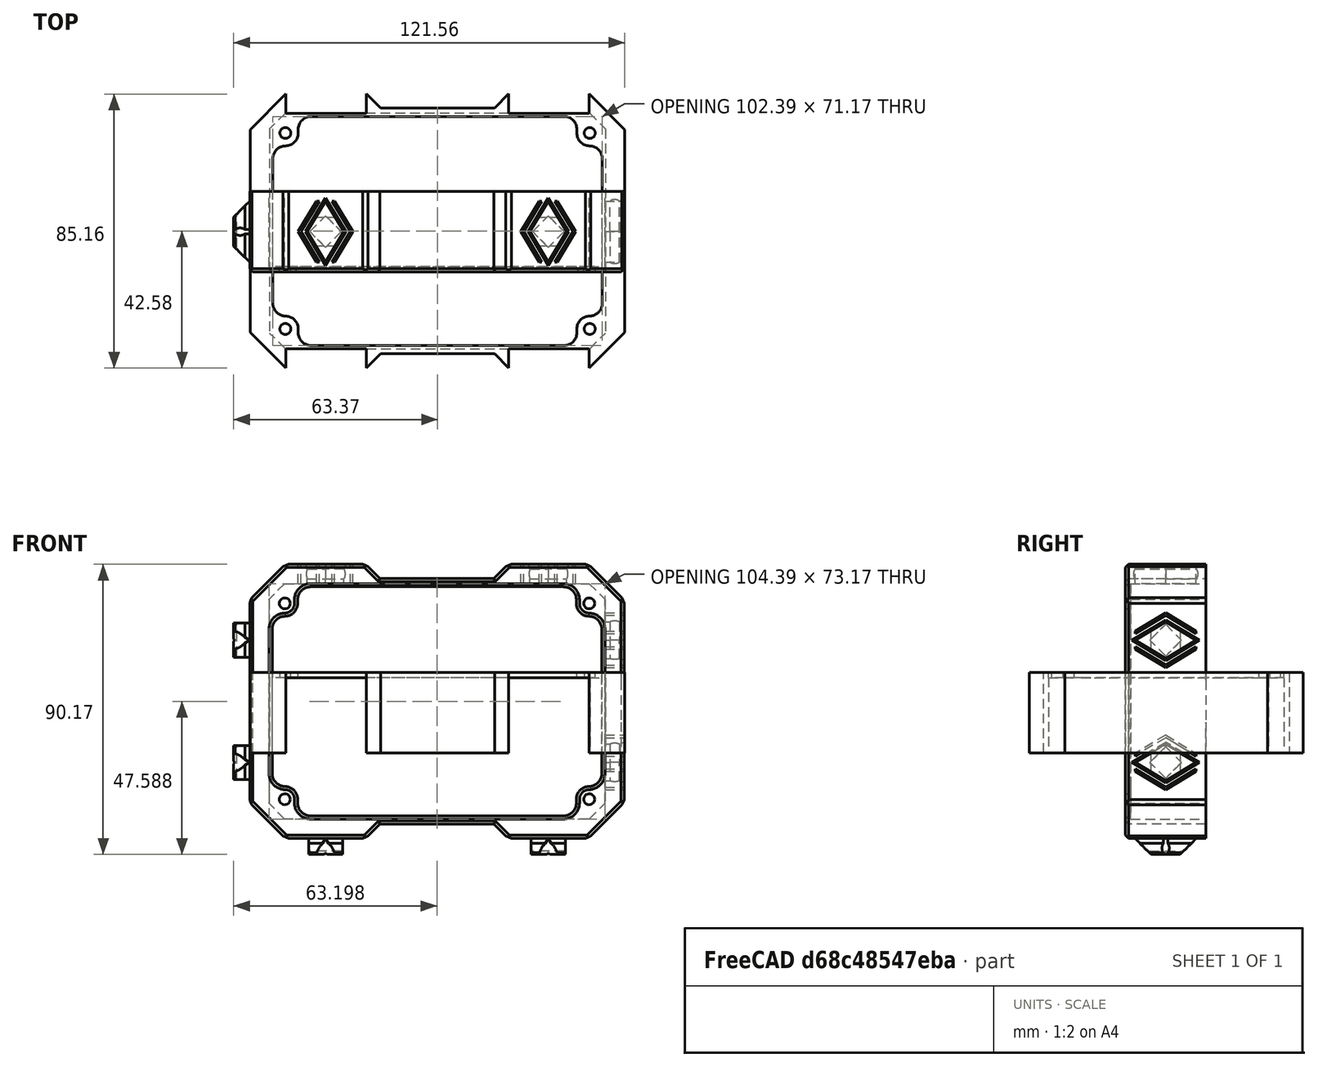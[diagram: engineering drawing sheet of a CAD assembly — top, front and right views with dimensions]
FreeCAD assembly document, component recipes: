
FREECAD ASSEMBLY — COMPONENT RECIPES ("K97-120_DockLink-Frame_front")

This assembly document has 3 components, labeled P0..P2 below (a component is one placed body or linked part). 3 of them carry a construction recipe — the FreeCAD feature program that regenerates the part from scratch, quoted from this document or its linked companion documents; the rest are supplied as boundary geometry only. No exploded tour is included for this assembly.
COMPONENT P0 — recipe-attached ("Body001", modeled in this document).
Construction recipe (the document's own serialized feature program — sketch geometry with constraints, then the solid features built on it; lengths are millimeters unless a unit is written):

FEATURE [Sketcher::SketchObject] Sketch
  ArcFitTolerance = 1e-06
  ExternalTypes = [0]
  FullyConstrained = true
  MakeInternals = false
  Placement = pos=(0,0,0.75) rot=(0,0,1;0rad)
  sketch-geometry (16):
    g0: ArcOfCircle [constr] CenterX=49.99 CenterY=30.66 CenterZ=0 NormalX=0 NormalY=0 NormalZ=1 AngleXU=0 Radius=2.00394 StartAngle=0.00171116 EndAngle=0.785083
    g1: LineSegment [constr] StartX=51.4075 StartY=32.0766 StartZ=0 EndX=47.58 EndY=35.9 EndZ=0
    g2: ArcOfCircle [constr] CenterX=46.17 CenterY=34.49 CenterZ=0 NormalX=0 NormalY=0 NormalZ=1 AngleXU=0 Radius=1.99404 StartAngle=0.785398 EndAngle=1.57287
    g3: LineSegment [constr] StartX=46.1659 StartY=36.484 StartZ=0 EndX=0 EndY=36.484 EndZ=0
    g4: LineSegment [constr] StartX=51.9939 StartY=30.6634 StartZ=0 EndX=51.9939 EndY=0 EndZ=0
    g5: Circle [constr] CenterX=47.29 CenterY=30.44 CenterZ=0 NormalX=0 NormalY=0 NormalZ=1 AngleXU=0 Radius=1.7
    g6: LineSegment StartX=0 StartY=38.184 StartZ=0 EndX=17.7 EndY=38.184 EndZ=0
    g7: LineSegment StartX=17.7 StartY=38.184 StartZ=0 EndX=22.1 EndY=42.584 EndZ=0
    g8: LineSegment StartX=22.1 StartY=42.584 StartZ=0 EndX=47.1 EndY=42.584 EndZ=0
    g9: LineSegment StartX=0 StartY=38.184 StartZ=0 EndX=0 EndY=36.584 EndZ=0
    g10: LineSegment StartX=0 StartY=36.584 StartZ=0 EndX=47.3197 EndY=36.584 EndZ=0
    g11: LineSegment StartX=47.3197 StartY=36.584 StartZ=0 EndX=52.1939 EndY=31.7149 EndZ=0
    g12: LineSegment StartX=52.1939 StartY=31.7149 StartZ=0 EndX=52.1939 EndY=0 EndZ=0
    g13: LineSegment StartX=47.1 StartY=42.584 StartZ=0 EndX=58.1939 EndY=31.5017 EndZ=0
    g14: LineSegment StartX=58.1939 StartY=31.5017 StartZ=0 EndX=58.1939 EndY=0 EndZ=0
    g15: LineSegment StartX=52.1939 StartY=0 StartZ=0 EndX=58.1939 EndY=0 EndZ=0
  constraints (53):
    c: Coincident(g1,g2)
    c: Coincident(g0,g1)
    c: Coincident(g3,g2)
    c: PointOnObject(g3,g-2)
    c: Horizontal(g3)
    c: Coincident(g4,g0)
    c: PointOnObject(g4,g-1)
    c: Vertical(g4)
    c: Distance(g5,g-1) = 30.44
    c: Distance(g5,g-2) = 47.29
    c: Diameter(g5) = 3.4
    c: Distance(g0,g-1) = 30.66
    c: Distance(g0,g-2) = 49.99
    c: Distance(g2,g-2) = 46.17
    c: Distance(g2,g-1) = 34.49
    c: Distance(g2,g1) = 1.53
    c: Distance(g0,g0) = 1.53
    c: Distance(g1,g1) = 5.41
    c: Angle(g1,g-1) = 0.784875
    c: Distance(g1,g-1) = 35.9
    c: Distance(g1,g-2) = 47.58
    c: PointOnObject(g6,g-2)
    c: Horizontal(g6)
    c: Coincident(g7,g6)
    c: Coincident(g8,g7)
    c: Horizontal(g8)
    c: Coincident(g9,g6)
    c: PointOnObject(g9,g-2)
    c: Coincident(g10,g9)
    c: Horizontal(g10)
    c: Coincident(g11,g10)
    c: Coincident(g12,g11)
    c: PointOnObject(g12,g-1)
    c: Vertical(g12)
    c: Distance(g12,g4) = 0.2
    c: Parallel(g11,g1)
    c: DistanceY(g9,g9) = 1.6
    c: Coincident(g13,g8)
    c: Coincident(g14,g13)
    c: PointOnObject(g14,g-1)
    c: Vertical(g14)
    c: Coincident(g15,g12)
    c: Coincident(g15,g14)
    c: DistanceX(g15,g15) = 6
    c: Parallel(g11,g13)
    c: Angle(g7,g6) = 2.35619
    c: Distance(g10,g8) = 6
    c: DistanceX(g8,g8) = 25
    c: Distance(g3,g10) = 0.1
    c: Distance(g11,g1) = 0.3
    c: DistanceX(g-1,g8) = 47.1
    c: Distance(g5,g-2) = 47.29
    c: Distance(g5,g-1) = 30.44
FEATURE [PartDesign::Pad] Pad
  Direction = (0,0,1)
  Length = 23.4
  Length2 = 10
  Placement = pos=(0,0,0.75) rot=(0,0,1;0rad)
  Profile = -> Sketch
  ReferenceAxis = -> Sketch [N_Axis]
  Refine = true
  Reversed = true
  SideType = 0
  Suppressed = false
  Type = 0
  Type2 = 0
FEATURE [PartDesign::Mirrored] Mirrored
  BaseFeature = -> Pad
  MirrorPlane = -> XZ_Plane
  Placement = pos=(0,0,0.75) rot=(0,0,1;0rad)
  Refine = true
  Suppressed = false
  TransformMode = 1
FEATURE [PartDesign::Mirrored] Mirrored001
  BaseFeature = -> Mirrored
  MirrorPlane = -> YZ_Plane
  Originals = -> [Mirrored]
  Placement = pos=(0,0,0.75) rot=(0,0,1;0rad)
  Refine = true
  Suppressed = false
  TransformMode = 1
FEATURE [Sketcher::SketchObject] Sketch001
  ArcFitTolerance = 1e-06
  AttachmentSupport = -> [Mirrored001]
  ExternalGeometry = -> [Mirrored001]
  ExternalTypes = [0,0,0,0,0,0,0,0,0,0,0,0,0,0,0,0]
  FullyConstrained = true
  MakeInternals = false
  MapMode = 5
  Placement = pos=(0,0,0.75) rot=(0,0,1;0rad)
  sketch-geometry (25):
    g0: LineSegment [constr] StartX=-47.29 StartY=30.44 StartZ=0 EndX=-47.29 EndY=-30.44 EndZ=0
    g1: LineSegment [constr] StartX=-47.29 StartY=-30.44 StartZ=0 EndX=47.29 EndY=-30.44 EndZ=0
    g2: LineSegment [constr] StartX=47.29 StartY=-30.44 StartZ=0 EndX=47.29 EndY=30.44 EndZ=0
    g3: LineSegment [constr] StartX=47.29 StartY=30.44 StartZ=0 EndX=-47.29 EndY=30.44 EndZ=0
    g4: GeomPoint [constr] X=0 Y=0 Z=0
    g5: Circle CenterX=47.29 CenterY=30.44 CenterZ=0 NormalX=0 NormalY=0 NormalZ=1 AngleXU=0 Radius=1.7
    g6: Circle CenterX=47.29 CenterY=-30.44 CenterZ=0 NormalX=0 NormalY=0 NormalZ=1 AngleXU=0 Radius=1.7
    g7: Circle CenterX=-47.29 CenterY=-30.44 CenterZ=0 NormalX=0 NormalY=0 NormalZ=1 AngleXU=0 Radius=1.7
    g8: Circle CenterX=-47.29 CenterY=30.44 CenterZ=0 NormalX=0 NormalY=0 NormalZ=1 AngleXU=0 Radius=1.7
    g9: ArcOfCircle CenterX=-47.29 CenterY=30.44 CenterZ=0 NormalX=0 NormalY=0 NormalZ=1 AngleXU=0 Radius=4 StartAngle=4.71239 EndAngle=6.28319
    g10: ArcOfCircle CenterX=47.29 CenterY=30.44 CenterZ=0 NormalX=0 NormalY=0 NormalZ=1 AngleXU=0 Radius=4 StartAngle=3.14159 EndAngle=4.71239
    g11: ArcOfCircle CenterX=47.29 CenterY=-30.44 CenterZ=0 NormalX=0 NormalY=0 NormalZ=1 AngleXU=0 Radius=4 StartAngle=1.5708 EndAngle=3.14159
    g12: ArcOfCircle CenterX=-47.29 CenterY=-30.44 CenterZ=0 NormalX=0 NormalY=0 NormalZ=1 AngleXU=0 Radius=4 StartAngle=0 EndAngle=1.5708
    g13: LineSegment StartX=-43.29 StartY=30.44 StartZ=0 EndX=-43.29 EndY=35.584 EndZ=0
    g14: LineSegment StartX=-43.29 StartY=35.584 StartZ=0 EndX=43.29 EndY=35.584 EndZ=0
    g15: LineSegment StartX=43.29 StartY=35.584 StartZ=0 EndX=43.29 EndY=30.44 EndZ=0
    g16: LineSegment StartX=47.29 StartY=26.44 StartZ=0 EndX=51.1939 EndY=26.44 EndZ=0
    g17: LineSegment StartX=47.29 StartY=-26.44 StartZ=0 EndX=51.1939 EndY=-26.44 EndZ=0
    g18: LineSegment StartX=51.1939 StartY=-26.44 StartZ=0 EndX=51.1939 EndY=26.44 EndZ=0
    g19: LineSegment StartX=43.29 StartY=-30.44 StartZ=0 EndX=43.29 EndY=-35.584 EndZ=0
    g20: LineSegment StartX=43.29 StartY=-35.584 StartZ=0 EndX=-43.29 EndY=-35.584 EndZ=0
    g21: LineSegment StartX=-43.29 StartY=-35.584 StartZ=0 EndX=-43.29 EndY=-30.44 EndZ=0
    g22: LineSegment StartX=-47.29 StartY=-26.44 StartZ=0 EndX=-51.1939 EndY=-26.44 EndZ=0
    g23: LineSegment StartX=-51.1939 StartY=-26.44 StartZ=0 EndX=-51.1939 EndY=26.44 EndZ=0
    g24: LineSegment StartX=-51.1939 StartY=26.44 StartZ=0 EndX=-47.29 EndY=26.44 EndZ=0
  constraints (68):
    c: Coincident(g0,g1)
    c: Coincident(g1,g2)
    c: Coincident(g2,g3)
    c: Coincident(g3,g0)
    c: Vertical(g0)
    c: Vertical(g2)
    c: Horizontal(g1)
    c: Horizontal(g3)
    c: Symmetric(g2,g0,g4)
    c: Coincident(g4,g-1)
    c: Distance(g2,g-2) = 47.29
    c: Distance(g3,g-1) = 30.44
    c: Coincident(g5,g2)
    c: Coincident(g6,g1)
    c: Coincident(g7,g0)
    c: Coincident(g8,g0)
    c: Equal(g8,g5)
    c: Equal(g5,g6)
    c: Equal(g7,g6)
    c: Diameter(g6) = 3.4
    c: Coincident(g9,g0)
    c: PointOnObject(g9,g0)
    c: PointOnObject(g9,g3)
    c: Coincident(g10,g2)
    c: PointOnObject(g10,g3)
    c: PointOnObject(g10,g2)
    c: Coincident(g11,g1)
    c: PointOnObject(g11,g1)
    c: PointOnObject(g11,g2)
    c: Coincident(g12,g0)
    c: PointOnObject(g12,g0)
    c: PointOnObject(g12,g1)
    c: Radius(g9) = 4
    c: Equal(g9,g10)
    c: Equal(g11,g10)
    c: Equal(g12,g9)
    c: Coincident(g13,g9)
    c: Vertical(g13)
    c: Coincident(g14,g13)
    c: Horizontal(g14)
    c: Coincident(g15,g14)
    c: Coincident(g15,g10)
    c: Coincident(g16,g10)
    c: Horizontal(g16)
    c: Coincident(g17,g11)
    c: Horizontal(g17)
    c: Coincident(g18,g17)
    c: Coincident(g18,g16)
    c: Vertical(g18)
    c: Coincident(g19,g11)
    c: Vertical(g19)
    c: Coincident(g20,g19)
    c: Horizontal(g20)
    c: Coincident(g21,g20)
    c: Coincident(g21,g12)
    c: Vertical(g21)
    c: Coincident(g22,g12)
    c: Horizontal(g22)
    c: Coincident(g23,g22)
    c: Vertical(g23)
    c: Coincident(g24,g23)
    c: Coincident(g24,g9)
    c: Horizontal(g24)
    c: Distance(g-7,g14) = 2.6
    c: Vertical(g15)
    c: Distance(g-11,g18) = 7
    c: Distance(g20,g-15) = 2.6
    c: Distance(g-5,g23) = 7
FEATURE [PartDesign::Pad] Pad001
  BaseFeature = -> Mirrored001
  Direction = (0,0,1)
  Length = 1.6
  Length2 = 10
  Placement = pos=(0,0,0.75) rot=(0,0,1;0rad)
  Profile = -> Sketch001
  ReferenceAxis = -> Sketch001 [N_Axis]
  Refine = true
  SideType = 0
  Suppressed = false
  Type = 0
  Type2 = 0
FEATURE [PartDesign::Fillet] Fillet
  Base = -> Pad001 [Edge107,Edge104,Edge108,Edge111,Edge112,Edge99,Edge103,Edge100]
  BaseFeature = -> Pad001
  Placement = pos=(0,0,0.75) rot=(0,0,1;0rad)
  Radius = 4
  Refine = true
  SupportTransform = false
  Suppressed = false
  UseAllEdges = false
FEATURE [Sketcher::SketchObject] Sketch002
  ArcFitTolerance = 1e-06
  AttachmentSupport = -> [Fillet]
  ExternalGeometry = -> [Fillet]
  ExternalTypes = [0,0,0,0,0,0,0,0]
  FullyConstrained = true
  MakeInternals = false
  MapMode = 5
  Placement = pos=(0,42.584,0.75) rot=(0,0.707107,0.707107;3.14159rad)
FEATURE [PartDesign::Pocket] Pocket
  BaseFeature = -> Fillet
  Direction = (0,-1,2e-16)
  Length = 6
  Length2 = 5
  Placement = pos=(0,0,0.75) rot=(0,0,1;0rad)
  Profile = -> Sketch002
  ReferenceAxis = -> Sketch002 [N_Axis]
  Refine = true
  SideType = 0
  Suppressed = false
  Type = 0
  Type2 = 0
FEATURE [Sketcher::SketchObject] Sketch003
  ArcFitTolerance = 1e-06
  AttachmentSupport = -> [Pocket]
  ExternalGeometry = -> [Pocket]
  ExternalTypes = [0,0,0,0,0,0,0,0]
  FullyConstrained = true
  MakeInternals = false
  MapMode = 5
  Placement = pos=(0,-42.584,0.75) rot=(1,0,0;1.5708rad)
FEATURE [PartDesign::Pocket] Pocket001
  BaseFeature = -> Pocket
  Direction = (0,1,-2e-16)
  Length = 6
  Length2 = 5
  Placement = pos=(0,0,0.75) rot=(0,0,1;0rad)
  Profile = -> Sketch003
  ReferenceAxis = -> Sketch003 [N_Axis]
  Refine = true
  SideType = 0
  Suppressed = false
  Type = 0
  Type2 = 0
FEATURE [PartDesign::Body] Body
  AllowCompound = true
  Group = -> [Sketch,Pad,Mirrored,Mirrored001,Sketch001,Pad001,Fillet,Sketch002,Pocket,Sketch003,Pocket001]
  Origin = -> Origin
  Tip = -> Pocket001
COMPONENT P1 — recipe-attached ("Body002", modeled in this document).
Construction recipe (the document's own serialized feature program — sketch geometry with constraints, then the solid features built on it; lengths are millimeters unless a unit is written):

FEATURE [PartDesign::FeatureBase] BaseFeature
  BaseFeature = -> Fusion
  Suppressed = false
FEATURE [PartDesign::Chamfer] Chamfer
  Angle = 45
  Base = -> BaseFeature [Edge61]
  BaseFeature = -> BaseFeature
  ChamferType = 0
  FlipDirection = false
  Refine = true
  Size = 1
  Size2 = 1
  SupportTransform = false
  Suppressed = false
  UseAllEdges = false
FEATURE [Sketcher::SketchObject] Sketch004
  ArcFitTolerance = 1e-06
  AttachmentSupport = -> [Chamfer]
  ExternalGeometry = -> [Chamfer]
  ExternalTypes = [0,0,0,0]
  FullyConstrained = true
  MakeInternals = false
  MapMode = 5
  Placement = pos=(-58.1939,1.68e-14,1.31e-14) rot=(0.57735,-0.57735,-0.57735;2.0944rad)
  sketch-geometry (6):
    g0: LineSegment StartX=-12.5 StartY=-16.6517 StartZ=0 EndX=12.5 EndY=-16.6517 EndZ=0
    g1: LineSegment StartX=-12.5 StartY=-3.64829 StartZ=0 EndX=12.5 EndY=-3.64829 EndZ=0
    g2: LineSegment StartX=-12.5 StartY=-3.64829 StartZ=0 EndX=-12.5 EndY=21.3517 EndZ=0
    g3: LineSegment StartX=12.5 StartY=21.3517 StartZ=0 EndX=12.5 EndY=-3.64829 EndZ=0
    g4: LineSegment StartX=-12.5 StartY=-16.6517 StartZ=0 EndX=-12.5 EndY=-41.6517 EndZ=0
    g5: LineSegment StartX=12.5 StartY=-16.6517 StartZ=0 EndX=12.5 EndY=-41.6517 EndZ=0
  constraints (16):
    c: PointOnObject(g0,g-5)
    c: PointOnObject(g0,g-6)
    c: Horizontal(g0)
    c: PointOnObject(g1,g-5)
    c: PointOnObject(g1,g-6)
    c: Horizontal(g1)
    c: DistanceY(g1,g-5) = 25
    c: DistanceY(g-5,g0) = 25
    c: Coincident(g2,g1)
    c: Coincident(g2,g-5)
    c: Coincident(g3,g-6)
    c: Coincident(g3,g1)
    c: Coincident(g4,g0)
    c: Coincident(g4,g-5)
    c: Coincident(g5,g0)
    c: Coincident(g5,g-6)
FEATURE [PartDesign::Pocket] Pocket002
  BaseFeature = -> Chamfer
  Direction = (1,0,0)
  Length = 6
  Length2 = 5
  Profile = -> Sketch004
  ReferenceAxis = -> Sketch004 [N_Axis]
  Refine = true
  SideType = 0
  Suppressed = false
  Type = 0
  Type2 = 0
FEATURE [Sketcher::SketchObject] Sketch005
  ArcFitTolerance = 1e-06
  AttachmentSupport = -> [Pocket002]
  ExternalGeometry = -> [Pocket002]
  ExternalTypes = [0,0,0,0]
  FullyConstrained = true
  MakeInternals = false
  MapMode = 5
  Placement = pos=(58.1939,0,0) rot=(0.57735,0.57735,0.57735;2.0944rad)
  sketch-geometry (6):
    g0: LineSegment StartX=-12.5 StartY=-3.64829 StartZ=0 EndX=12.5 EndY=-3.64829 EndZ=0
    g1: LineSegment StartX=-12.5 StartY=-16.6517 StartZ=0 EndX=12.5 EndY=-16.6517 EndZ=0
    g2: LineSegment StartX=-12.5 StartY=21.3517 StartZ=0 EndX=-12.5 EndY=-3.64829 EndZ=0
    g3: LineSegment StartX=12.5 StartY=21.3517 StartZ=0 EndX=12.5 EndY=-3.64829 EndZ=0
    g4: LineSegment StartX=-12.5 StartY=-16.6517 StartZ=0 EndX=-12.5 EndY=-41.6517 EndZ=0
    g5: LineSegment StartX=12.5 StartY=-16.6517 StartZ=0 EndX=12.5 EndY=-41.6517 EndZ=0
  constraints (16):
    c: PointOnObject(g0,g-5)
    c: PointOnObject(g0,g-6)
    c: Horizontal(g0)
    c: PointOnObject(g1,g-5)
    c: PointOnObject(g1,g-6)
    c: Horizontal(g1)
    c: DistanceY(g-6,g1) = 25
    c: DistanceY(g0,g-6) = 25
    c: Coincident(g2,g-5)
    c: Coincident(g2,g0)
    c: Coincident(g3,g-6)
    c: Coincident(g3,g0)
    c: Coincident(g4,g1)
    c: Coincident(g4,g-5)
    c: Coincident(g5,g1)
    c: Coincident(g5,g-6)
FEATURE [PartDesign::Pocket] Pocket003
  BaseFeature = -> Pocket002
  Direction = (-1,0,0)
  Length = 6
  Length2 = 5
  Profile = -> Sketch005
  ReferenceAxis = -> Sketch005 [N_Axis]
  Refine = true
  SideType = 0
  Suppressed = false
  Type = 0
  Type2 = 0
FEATURE [PartDesign::Body] Body002
  AllowCompound = true
  BaseFeature = -> Fusion
  Group = -> [BaseFeature,Chamfer,Sketch004,Pocket002,Sketch005,Pocket003]
  Origin = -> Origin004
  Placement = pos=(-0.172249,-0.214718,3.51786) rot=(0,0,1;0rad)
  Tip = -> Pocket003
COMPONENT P2 — recipe-attached ("K97-120_DockLink-Frame_front", modeled in this document).
Construction recipe (the document's own serialized feature program — sketch geometry with constraints, then the solid features built on it; lengths are millimeters unless a unit is written):

FEATURE [PartDesign::FeatureBase] BaseFeature001
  BaseFeature = -> Fusion001
  Suppressed = false
FEATURE [PartDesign::Chamfer] Chamfer001
  Angle = 45
  Base = -> BaseFeature001 [Edge161,Edge160,Edge159,Edge158,Edge157,Edge156,Edge155,Edge154,Edge153,Edge3,Edge6,Edge15,Edge17,Edge20,Edge24,Edge32]
  BaseFeature = -> BaseFeature001
  ChamferType = 0
  FlipDirection = false
  Refine = true
  Size = 1
  Size2 = 1
  SupportTransform = false
  Suppressed = false
  UseAllEdges = false
FEATURE [PartDesign::Chamfer] Chamfer002
  Angle = 45
  Base = -> Chamfer001 [Edge216,Edge229,Edge232,Edge254,Edge87,Edge11,Edge212,Edge204,Edge202,Edge80,Edge4,Edge1]
  BaseFeature = -> Chamfer001
  ChamferType = 0
  FlipDirection = false
  Refine = true
  Size = 1
  Size2 = 1
  SupportTransform = false
  Suppressed = false
  UseAllEdges = false
FEATURE [PartDesign::Body] Body003  label="K97-120_DockLink-Frame_front"
  AllowCompound = true
  BaseFeature = -> Fusion001
  Group = -> [BaseFeature001,Chamfer001,Chamfer002]
  Origin = -> Origin006
  Tip = -> Chamfer002
PROVENANCE & LICENSES
A FreeCAD (.FCStd) document from a public repository crawl; recipes are the document's own serialized feature recipes (and, for linked parts, companion documents' recipes).
License: mit.
